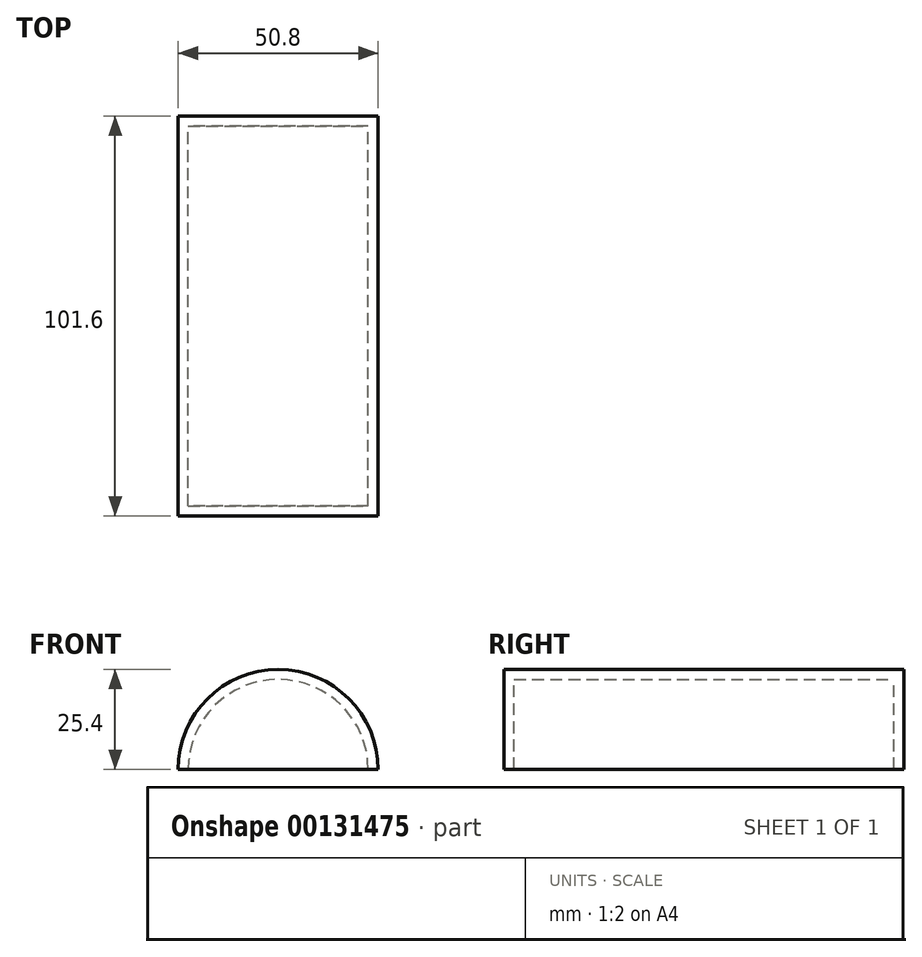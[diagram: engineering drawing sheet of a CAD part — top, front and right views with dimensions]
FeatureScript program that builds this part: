
annotation { "Feature Type Name" : "Feature", "Feature Type Description" : "" }
export const myFeature = defineFeature(function(context is Context, id is Id, definition is map)
    precondition{}
    {
        {
            var Q0;
            Q0=qCreatedBy(makeId("Front.planeOp"),FACE);
            var sketch = newSketch(context, id + "F0", { "sketchPlane" : qUnion([Q0])});
            skArc(sketch, "E0", {"start": v(25.4, 0) * mm, "mid": v(0, 25.4) * mm, "end": v(-25.4, 0) * mm});
            skLineSegment(sketch, "E1", {"start": v(-25.4, 0) * mm, "end": v(25.4, 0) * mm});
            skSolve(sketch);
        }
        {
            var Q0;
            Q0 = qSketchRegion(id + "F0", true);
            extrude(context, id + "F1", {"entities" : qUnion([Q0]), "depth" : 101.6 * mm});
        }
        {
            var Q0;
            Q0=makeQuery(id+"F1.opExtrude","SWEPT_FACE",FACE,{"disambiguationData":[OSD([sQuery(id+"F0.wireOp",EDGE,"E1")])]});
            shell(context, id + "F2", {"entities" : qUnion([Q0]), "thickness" : 2.54 * mm});
        }
    });
